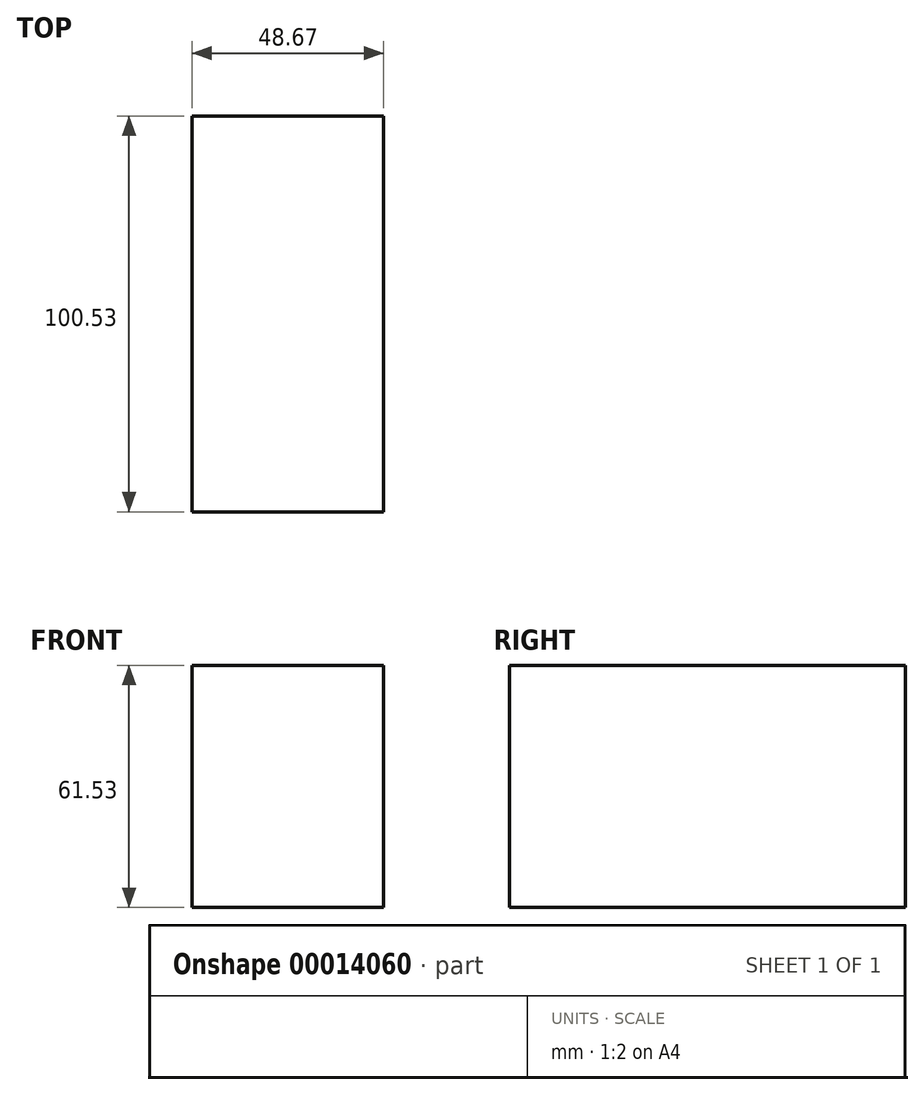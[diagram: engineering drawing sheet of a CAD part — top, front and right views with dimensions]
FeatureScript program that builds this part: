
annotation { "Feature Type Name" : "Feature", "Feature Type Description" : "" }
export const myFeature = defineFeature(function(context is Context, id is Id, definition is map)
    precondition{}
    {
        {
            var Q0;
            Q0=qCreatedBy(makeId("Top.planeOp"),FACE);
            var sketch = newSketch(context, id + "F0", { "sketchPlane" : qUnion([Q0])});
            skLineSegment(sketch, "E0.bottom", {"start": v(-131.82, 46.24) * mm, "end": v(-83.15, 46.24) * mm});
            skLineSegment(sketch, "E0.top", {"start": v(-131.82, -49.34) * mm, "end": v(-83.15, -49.34) * mm});
            skLineSegment(sketch, "E0.left", {"start": v(-131.82, 46.24) * mm, "end": v(-131.82, -49.34) * mm});
            skLineSegment(sketch, "E0.right", {"start": v(-83.15, 46.24) * mm, "end": v(-83.15, -49.34) * mm});
            skSolve(sketch);
        }
        {
            var Q0;
            Q0=sQuery(id+"F0.wireOp",EDGE,"E0.top");
            extrude(context, id + "F1", {"bodyType" : ToolBodyType.SURFACE, "surfaceEntities" : qUnion([Q0]), "depth" : 61.53 * mm});
        }
        {
            var Q0;
            Q0=makeQuery(id+"F1.opExtrude","SWEPT_FACE",FACE,{"disambiguationData":[OSD([sQuery(id+"F0.wireOp",EDGE,"E0.top")])]});
            extrude(context, id + "F2", {"entities" : qUnion([Q0]), "depth" : 100.54 * mm});
        }
    });
